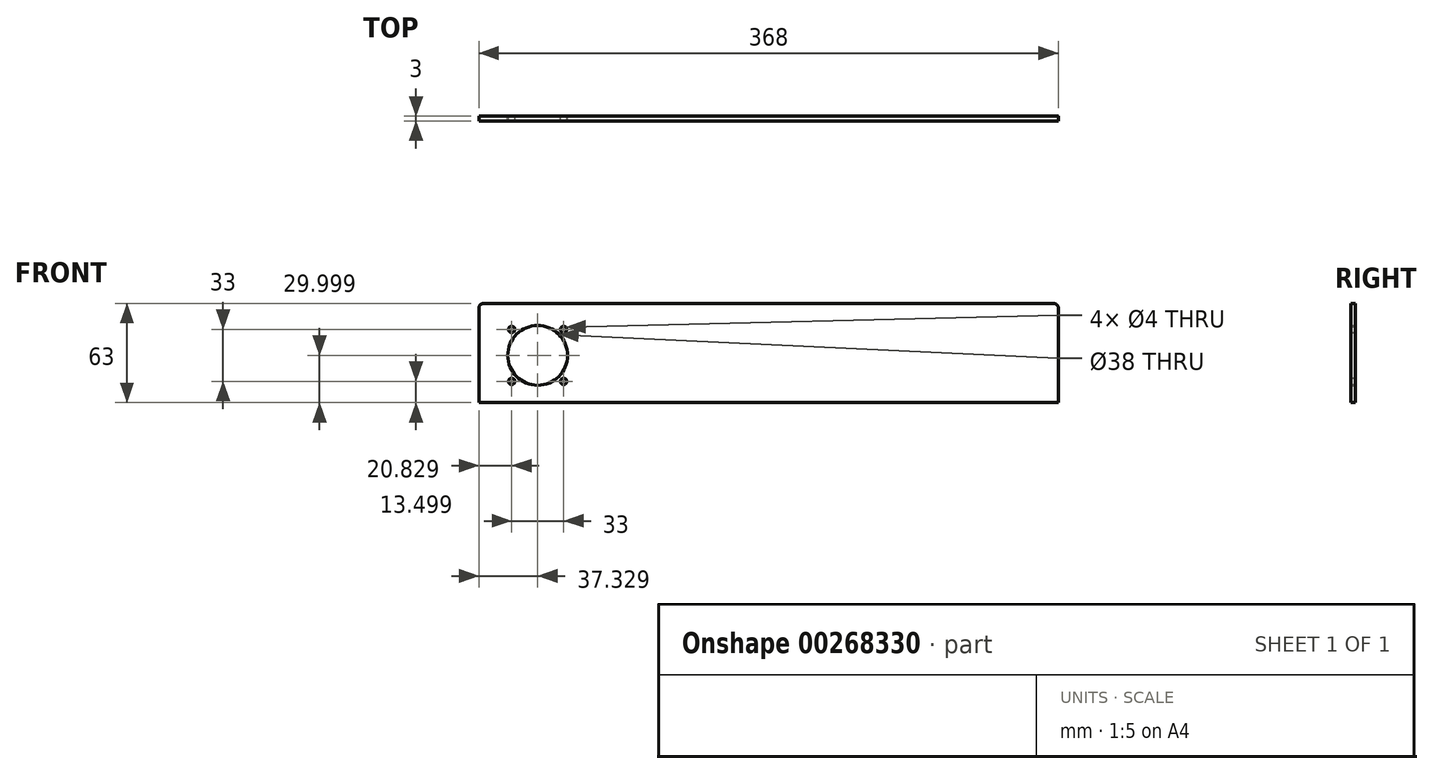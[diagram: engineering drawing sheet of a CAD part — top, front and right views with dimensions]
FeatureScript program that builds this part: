
annotation { "Feature Type Name" : "Feature", "Feature Type Description" : "" }
export const myFeature = defineFeature(function(context is Context, id is Id, definition is map)
    precondition{}
    {
        {
            var Q0;
            Q0=qCreatedBy(makeId("Front.planeOp"),FACE);
            var sketch = newSketch(context, id + "F0", { "sketchPlane" : qUnion([Q0])});
            skLineSegment(sketch, "E0.bottom", {"start": v(-185.79, -51.45) * mm, "end": v(176.21, -51.45) * mm});
            skLineSegment(sketch, "E0.top", {"start": v(-188.79, -114.45) * mm, "end": v(179.21, -114.45) * mm});
            skLineSegment(sketch, "E0.left", {"start": v(-188.79, -54.45) * mm, "end": v(-188.79, -114.45) * mm});
            skLineSegment(sketch, "E0.right", {"start": v(179.21, -54.45) * mm, "end": v(179.21, -114.45) * mm});
            skPoint(sketch, "E1.visualSharp", {"position": v(-188.79, -51.45) * mm});
            skArc(sketch, "E1.filletArc", {"start": v(-185.79, -51.45) * mm, "mid": v(-187.9, -52.33) * mm, "end": v(-188.79, -54.45) * mm});
            skPoint(sketch, "E2.visualSharp", {"position": v(179.21, -51.45) * mm});
            skArc(sketch, "E2.filletArc", {"start": v(179.21, -54.45) * mm, "mid": v(178.33, -52.33) * mm, "end": v(176.21, -51.45) * mm});
            skCircle(sketch, "E3", {"center": v(-151.46, -84.45) * mm, "radius": 19 * mm});
            skPoint(sketch, "E3.centerSnap0", {"position": v(179.21, -84.45) * mm});
            skCircle(sketch, "E4", {"center": v(-134.96, -67.95) * mm, "radius": 2 * mm});
            skCircle(sketch, "E5", {"center": v(-167.96, -67.95) * mm, "radius": 2 * mm});
            skCircle(sketch, "E6", {"center": v(-167.96, -100.95) * mm, "radius": 2 * mm});
            skCircle(sketch, "E7", {"center": v(-134.96, -100.95) * mm, "radius": 2 * mm});
            skSolve(sketch);
        }
        {
            var Q0;
            Q0=qSketchRegion(id+"F0",true);
            extrude(context, id + "F1", {"entities" : qUnion([Q0]), "depth" : 3 * mm});
        }
    });
